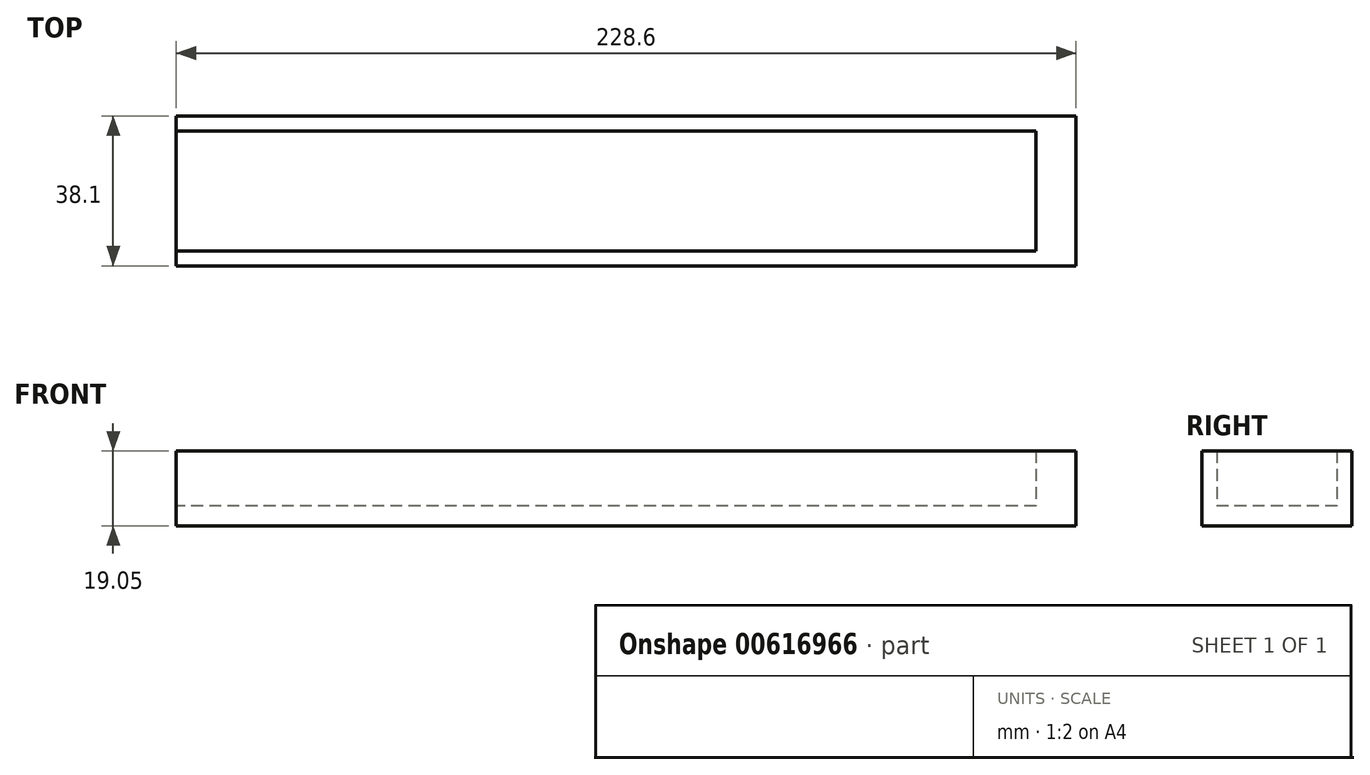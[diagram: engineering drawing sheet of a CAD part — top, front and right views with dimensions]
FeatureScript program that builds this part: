
annotation { "Feature Type Name" : "Feature", "Feature Type Description" : "" }
export const myFeature = defineFeature(function(context is Context, id is Id, definition is map)
    precondition{}
    {
        {
            var Q0;
            Q0=qCreatedBy(makeId("Right.planeOp"),FACE);
            var sketch = newSketch(context, id + "F0", { "sketchPlane" : qUnion([Q0])});
            skLineSegment(sketch, "E0", {"start": v(-41.52, 7.97) * mm, "end": v(-3.42, 7.97) * mm});
            skLineSegment(sketch, "E1", {"start": v(-3.42, 7.97) * mm, "end": v(-3.42, 27.02) * mm});
            skLineSegment(sketch, "E2", {"start": v(-41.52, 27.02) * mm, "end": v(-41.52, 7.97) * mm});
            skLineSegment(sketch, "E3", {"start": v(-41.52, 27.02) * mm, "end": v(-37.7, 27.02) * mm});
            skLineSegment(sketch, "E4", {"start": v(-3.42, 27.02) * mm, "end": v(-7.23, 27.02) * mm});
            skLineSegment(sketch, "E5", {"start": v(-7.23, 27.02) * mm, "end": v(-7.23, 13.05) * mm});
            skLineSegment(sketch, "E6", {"start": v(-7.23, 13.05) * mm, "end": v(-37.7, 13.05) * mm});
            skLineSegment(sketch, "E7", {"start": v(-37.7, 13.05) * mm, "end": v(-37.7, 27.02) * mm});
            skSolve(sketch);
        }
        {
            var Q0;
            Q0 = qSketchRegion(id + "F0", true);
            extrude(context, id + "F1", {"entities" : qUnion([Q0]), "depth" : 228.6 * mm, "offsetDistance" : 25.4 * mm});
        }
        {
            var Q0;
            Q0 = qSketchRegion(id + "F0", true);
            extrude(context, id + "F2", {"entities" : qUnion([Q0]), "operationType" : NewBodyOperationType.ADD, "depth" : 228.6 * mm, "offsetDistance" : 25.4 * mm});
        }
        {
            var Q0;
            Q0=makeQuery(id+"F1.opExtrude","SWEPT_FACE",FACE,{"disambiguationData":[OSD([sQuery(id+"F0.wireOp",EDGE,"E6")])]});
            var sketch = newSketch(context, id + "F3", { "sketchPlane" : qUnion([Q0])});
            skLineSegment(sketch, "E8", {"start": v(228.6, -7.23) * mm, "end": v(218.44, -7.23) * mm});
            skLineSegment(sketch, "E9", {"start": v(218.44, -7.23) * mm, "end": v(218.44, -37.7) * mm});
            skLineSegment(sketch, "E10", {"start": v(218.44, -37.7) * mm, "end": v(228.6, -37.7) * mm});
            skLineSegment(sketch, "E11", {"start": v(228.6, -37.7) * mm, "end": v(228.6, -7.23) * mm});
            skSolve(sketch);
        }
        {
            var Q0;
            Q0 = qSketchRegion(id + "F3", true);
            extrude(context, id + "F4", {"entities" : qUnion([Q0]), "operationType" : NewBodyOperationType.ADD, "depth" : 13.97 * mm, "offsetDistance" : 25.4 * mm});
        }
        {
            var Q0;
            Q0=makeQuery(id+"F1.opExtrude","SWEPT_BODY",BODY,{"disambiguationData":[OSD([sQuery(id+"F0.wireOp",EDGE,"E0"),sQuery(id+"F0.wireOp",EDGE,"E1"),sQuery(id+"F0.wireOp",EDGE,"E2"),sQuery(id+"F0.wireOp",EDGE,"E3"),sQuery(id+"F0.wireOp",EDGE,"E4"),sQuery(id+"F0.wireOp",EDGE,"E5"),sQuery(id+"F0.wireOp",EDGE,"E6"),sQuery(id+"F0.wireOp",EDGE,"E7")])]});
            transform(context, id + "F5", {"entities" : qUnion([Q0]), "transformType" : TransformType.TRANSLATION_3D, "dx" : 0 * mm, "dy" : 0 * mm, "dz" : 0 * mm, "makeCopy" : true});
        }
        {
            var Q0;
            Q0=makeQuery(id+"F5.opPattern","COPY",BODY,{"derivedFrom":makeQuery(id+"F1.opExtrude","SWEPT_BODY",BODY,{"disambiguationData":[OSD([sQuery(id+"F0.wireOp",EDGE,"E0"),sQuery(id+"F0.wireOp",EDGE,"E1"),sQuery(id+"F0.wireOp",EDGE,"E2"),sQuery(id+"F0.wireOp",EDGE,"E3"),sQuery(id+"F0.wireOp",EDGE,"E4"),sQuery(id+"F0.wireOp",EDGE,"E5"),sQuery(id+"F0.wireOp",EDGE,"E6"),sQuery(id+"F0.wireOp",EDGE,"E7")])]}),"instanceName":"1"});
            deleteBodies(context, id + "F6", {"entities" : qUnion([Q0])});
        }
    });
